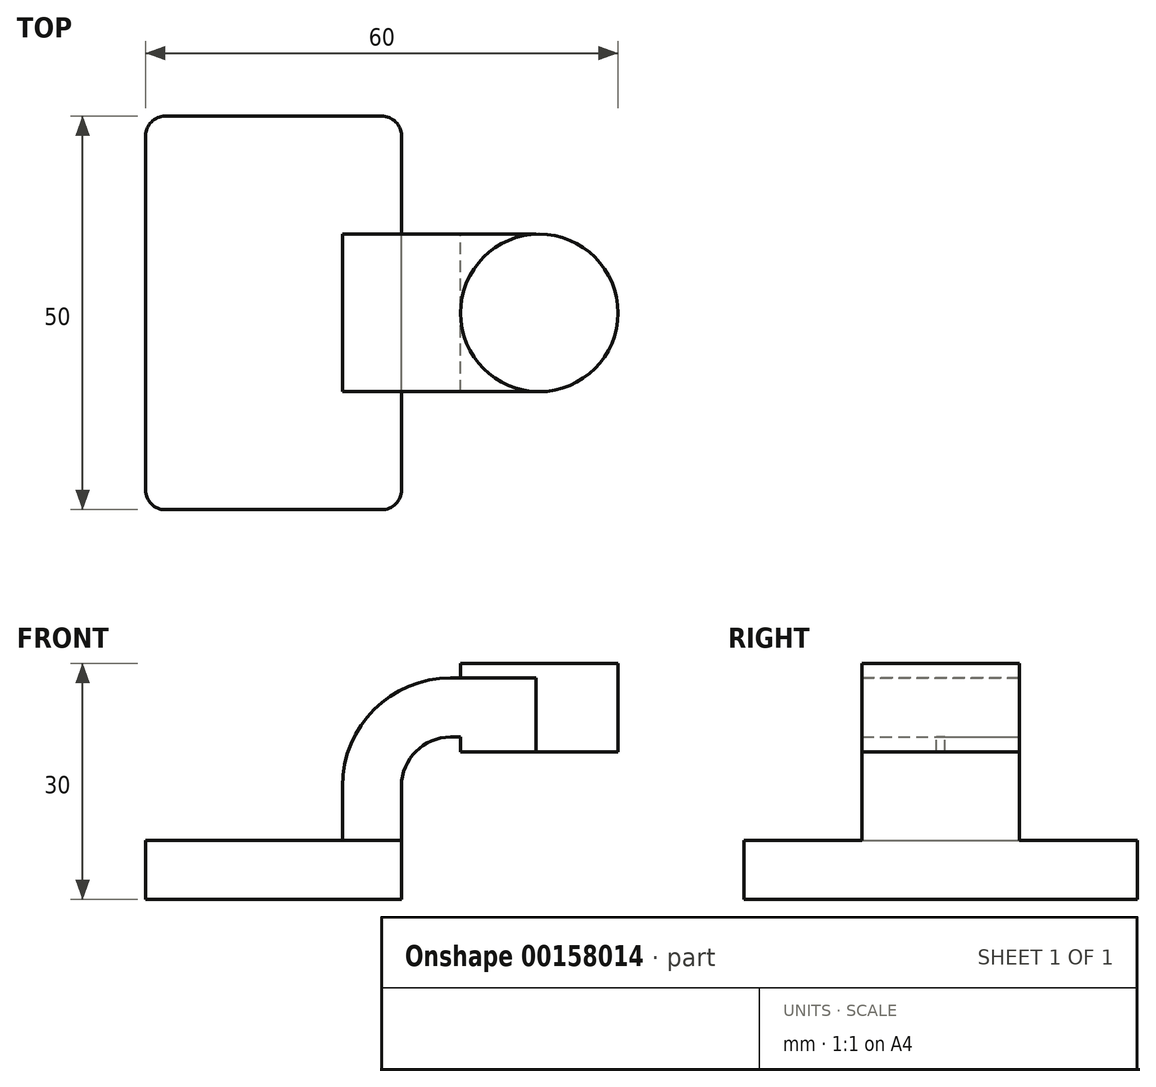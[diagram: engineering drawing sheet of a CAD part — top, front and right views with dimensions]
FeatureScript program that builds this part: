
annotation { "Feature Type Name" : "Feature", "Feature Type Description" : "" }
export const myFeature = defineFeature(function(context is Context, id is Id, definition is map)
    precondition{}
    {
        {
            var Q0;
            Q0=qCreatedBy(makeId("Front.planeOp"),FACE);
            var sketch = newSketch(context, id + "F0", { "sketchPlane" : qUnion([Q0])});
            skLineSegment(sketch, "E0.bottom", {"start": v(-16.25, 3.75) * mm, "end": v(16.25, 3.75) * mm});
            skLineSegment(sketch, "E0.top", {"start": v(-16.25, -3.75) * mm, "end": v(16.25, -3.75) * mm});
            skLineSegment(sketch, "E0.left", {"start": v(-16.25, 3.75) * mm, "end": v(-16.25, -3.75) * mm});
            skLineSegment(sketch, "E0.right", {"start": v(16.25, 3.75) * mm, "end": v(16.25, -3.75) * mm});
            skPoint(sketch, "E0.middle", {"position": v(0, 0) * mm});
            skLineSegment(sketch, "E1.bottom", {"start": v(43.75, 15) * mm, "end": v(23.75, 15) * mm});
            skLineSegment(sketch, "E1.top", {"start": v(43.75, 26.25) * mm, "end": v(23.75, 26.25) * mm});
            skLineSegment(sketch, "E1.left", {"start": v(43.75, 15) * mm, "end": v(43.75, 26.25) * mm});
            skLineSegment(sketch, "E1.right", {"start": v(23.75, 15) * mm, "end": v(23.75, 26.25) * mm});
            skPoint(sketch, "E1.middle", {"position": v(33.75, 20.63) * mm});
            skLineSegment(sketch, "E2", {"start": v(16.25, 3.75) * mm, "end": v(16.25, 10.63) * mm});
            skArc(sketch, "E3", {"start": v(16.25, 10.63) * mm, "mid": v(18.08, 15.05) * mm, "end": v(22.5, 16.88) * mm});
            skLineSegment(sketch, "E4", {"start": v(22.5, 16.88) * mm, "end": v(33.7, 16.88) * mm});
            skLineSegment(sketch, "E5.0", {"start": v(22.5, 24.38) * mm, "end": v(33.74, 24.38) * mm});
            skArc(sketch, "E5.1", {"start": v(8.75, 10.63) * mm, "mid": v(12.78, 20.35) * mm, "end": v(22.5, 24.38) * mm});
            skLineSegment(sketch, "E5.2", {"start": v(8.75, 3.75) * mm, "end": v(8.75, 10.63) * mm});
            skLineSegment(sketch, "E6", {"start": v(33.74, 26.25) * mm, "end": v(33.74, 15) * mm});
            skFitSpline(sketch, "E7", {"points": [v(-16.25, 3.75) * mm, v(22.5, 24.38) * mm], "startDerivative": vector(20.25, 36.77) * mm, "endDerivative": vector(56.74, -6.66) * mm});
            skSolve(sketch);
        }
        {
            var Q0;
            Q0=makeQuery(id+"F0.imprint","IMPRINT",FACE,{"disambiguationData":[TD([[makeQuery(id+"F0.imprint","IMPRINT",EDGE,{"derivedFrom":sQuery(id+"F0.wireOp",EDGE,"E0.top")}),1.0]])]});
            extrude(context, id + "F1", {"entities" : qUnion([Q0]), "endBound" : BoundingType.SYMMETRIC, "depth" : 50 * mm});
        }
        {
            var Q0;
            {var subQ2=sQuery(id+"F0.wireOp",EDGE,"E2");Q0=makeQuery(id+"F0.imprint","IMPRINT",FACE,{"disambiguationData":[TD([[makeQuery(id+"F0.imprint","IMPRINT",EDGE,{"derivedFrom":subQ2}),1.0]])]});}
            var Q1;
            {var subQ0=sQuery(id+"F0.wireOp",EDGE,"E1.right");var subQ1=sQuery(id+"F0.wireOp",EDGE,"E1.bottom");var subQ2=makeQuery(id+"F0.imprint","INTERSECT",VERTEX,{"derivedFrom":[subQ1,subQ0]});Q1=makeQuery(id+"F0.imprint","IMPRINT",FACE,{"disambiguationData":[TD([[makeQuery(id+"F0.imprint","IMPRINT",EDGE,{"disambiguationData":[TD([[subQ2,1.0]])],"derivedFrom":subQ1}),-1.0]])]});}
            extrude(context, id + "F2", {"entities" : qUnion([Q0, Q1]), "operationType" : NewBodyOperationType.ADD, "endBound" : BoundingType.SYMMETRIC, "depth" : 20 * mm});
        }
        {
            var Q0;
            Q0=makeQuery(id+"F0.imprint","IMPRINT",FACE,{"disambiguationData":[TD([[makeQuery(id+"F0.imprint","IMPRINT",EDGE,{"derivedFrom":sQuery(id+"F0.wireOp",EDGE,"E5.1")}),1.0]])]});
            extrude(context, id + "F3", {"entities" : qUnion([Q0]), "operationType" : NewBodyOperationType.ADD, "endBound" : BoundingType.SYMMETRIC, "depth" : 6.25 * mm});
        }
        {
            var Q0;
            {var subQ4=sQuery(id+"F0.wireOp",EDGE,"E1.left");Q0=makeQuery(id+"F0.imprint","IMPRINT",FACE,{"disambiguationData":[TD([[makeQuery(id+"F0.imprint","IMPRINT",EDGE,{"derivedFrom":subQ4}),1.0]])]});}
            var Q1;
            Q1=sQuery(id+"F0.wireOp",EDGE,"E6");
            revolve(context, id + "F4", {"operationType" : NewBodyOperationType.ADD, "entities" : qUnion([Q0]), "axis" : qUnion([Q1]), "revolveType" : RevolveType.FULL});
        }
        {
            var Q0;
            Q0=makeQuery(id+"F1.opExtrude","CAP_EDGE",EDGE,{"disambiguationData":[OSD([sQuery(id+"F0.wireOp",EDGE,"E0.right")])],"isStart":true});
            var Q1;
            Q1=makeQuery(id+"F1.opExtrude","CAP_EDGE",EDGE,{"disambiguationData":[OSD([sQuery(id+"F0.wireOp",EDGE,"E0.left")])],"isStart":true});
            var Q2;
            Q2=makeQuery(id+"F1.opExtrude","CAP_EDGE",EDGE,{"disambiguationData":[OSD([sQuery(id+"F0.wireOp",EDGE,"E0.left")])],"isStart":false});
            var Q3;
            Q3=makeQuery(id+"F1.opExtrude","CAP_EDGE",EDGE,{"disambiguationData":[OSD([sQuery(id+"F0.wireOp",EDGE,"E0.right")])],"isStart":false});
            fillet(context, id + "F5", {"entities" : qUnion([Q0, Q1, Q2, Q3]), "radius" : 2.5 * mm, "tangentPropagation" : true, "allowEdgeOverflow" : false});
        }
    });
